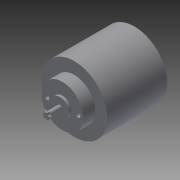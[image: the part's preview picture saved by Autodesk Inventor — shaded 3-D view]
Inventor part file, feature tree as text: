
AUTODESK INVENTOR PART (.ipt)
format: ipt  version: 2015 (Build 190159000, 159)  size: 171,520 bytes
history: native  units: in
note: dims shown in document units (in); Inventor stores cm internally (conversion verified against a paired STEP export)
features: extrude x9, sketch x9, plane x1
ambient origin geometry x8: Origin, YZ Plane, XZ Plane, XY Plane, X Axis, Y Axis, Z Axis, Center Point
bodies: Solid1 (feature_tree)
feature tree (19):
  extrude  "Extrusion1"  Depth=2.5in TaperAngle=0.0deg
  extrude  "Extrusion2"  Depth=0.5in TaperAngle=0.0deg
  extrude  "Extrusion3"  Depth=0.1in TaperAngle=0.0deg
  extrude  "Extrusion4"  TaperAngle=0.0deg  [1 undecoded]
  plane  "Work Plane1"
  extrude  "Extrusion6"  Depth=0.2in
  extrude  "Extrusion7"  Depth=0.65in
  extrude  "Extrusion8"  Depth=1.5in TaperAngle=0.0deg
  extrude  "Extrusion9"  Depth=0.01in TaperAngle=0.0deg
  extrude  "Extrusion10"  Depth=0.1in
  sketch  "Sketch1"  dims[d0=2.75in d1=2.5in d2=0.0in]
  sketch  "Sketch2"  dims[d3=1.75in d4=0.5in d5=0.0in]
  sketch  "Sketch3"  dims[d6=0.75in d7=0.1in d8=0.0in]
  sketch  "Sketch4"  dims[d9=0.5in d10=0.0in d11=0.0in]
  sketch  "Sketch6"  dims[d14=0.65in d15=0.2in]
  sketch  "Sketch7"  dims[d16=1.5in d17=0.0in d18=0.65in]
  sketch  "Sketch8"  dims[d19=0.2in d20=1.5in d21=0.0in]
  sketch  "Sketch9"  dims[d22=2.0in d23=0.0in d24=0.01in d25=0.0in]
  sketch  "Sketch10"  dims[d26=0.1875in d27=0.3125in d28=2.3622in d30=360.0deg d32=2.3622in d34=360.0deg d36=2.3622in d38=360.0deg d40=2.3622in d42=360.0deg d44=0.1in d45=0.0in]
note: 1 required parameter value undecoded (feature->parameter linkage not recoverable at this tier; creation-order binding heuristic only, values carry confidence <= 0.55)
